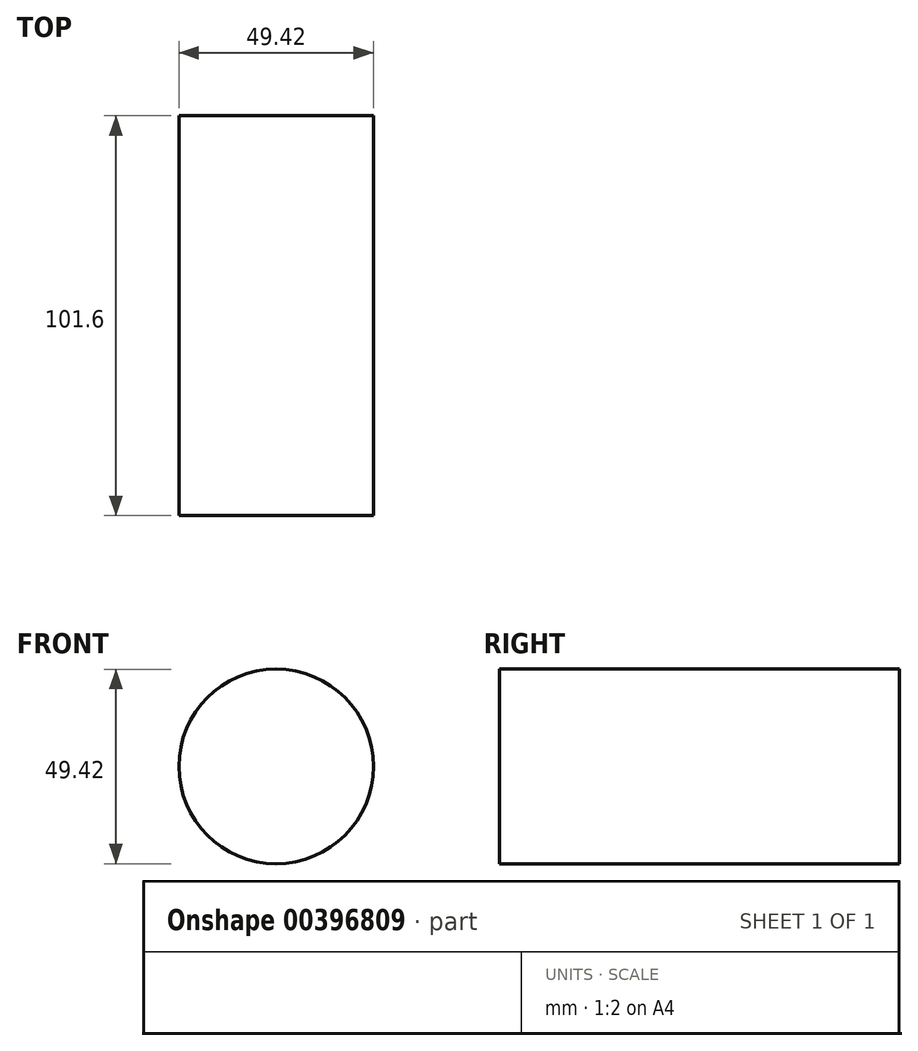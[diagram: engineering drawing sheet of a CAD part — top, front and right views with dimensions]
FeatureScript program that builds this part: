
annotation { "Feature Type Name" : "Feature", "Feature Type Description" : "" }
export const myFeature = defineFeature(function(context is Context, id is Id, definition is map)
    precondition{}
    {
        {
            var Q0;
            Q0=qCreatedBy(makeId("Front.planeOp"),FACE);
            var sketch = newSketch(context, id + "F0", { "sketchPlane" : qUnion([Q0])});
            skCircle(sketch, "E0", {"center": v(-55.95, 12.8) * mm, "radius": 24.71 * mm});
            skSolve(sketch);
        }
        {
            var Q0;
            Q0=makeQuery(id+"F0.imprint","IMPRINT",FACE,{"disambiguationData":[TD([[makeQuery(id+"F0.imprint","IMPRINT",EDGE,{"derivedFrom":sQuery(id+"F0.wireOp",EDGE,"E0")}),1.0]])]});
            extrude(context, id + "F1", {"entities" : qUnion([Q0]), "depth" : 101.6 * mm});
        }
    });
